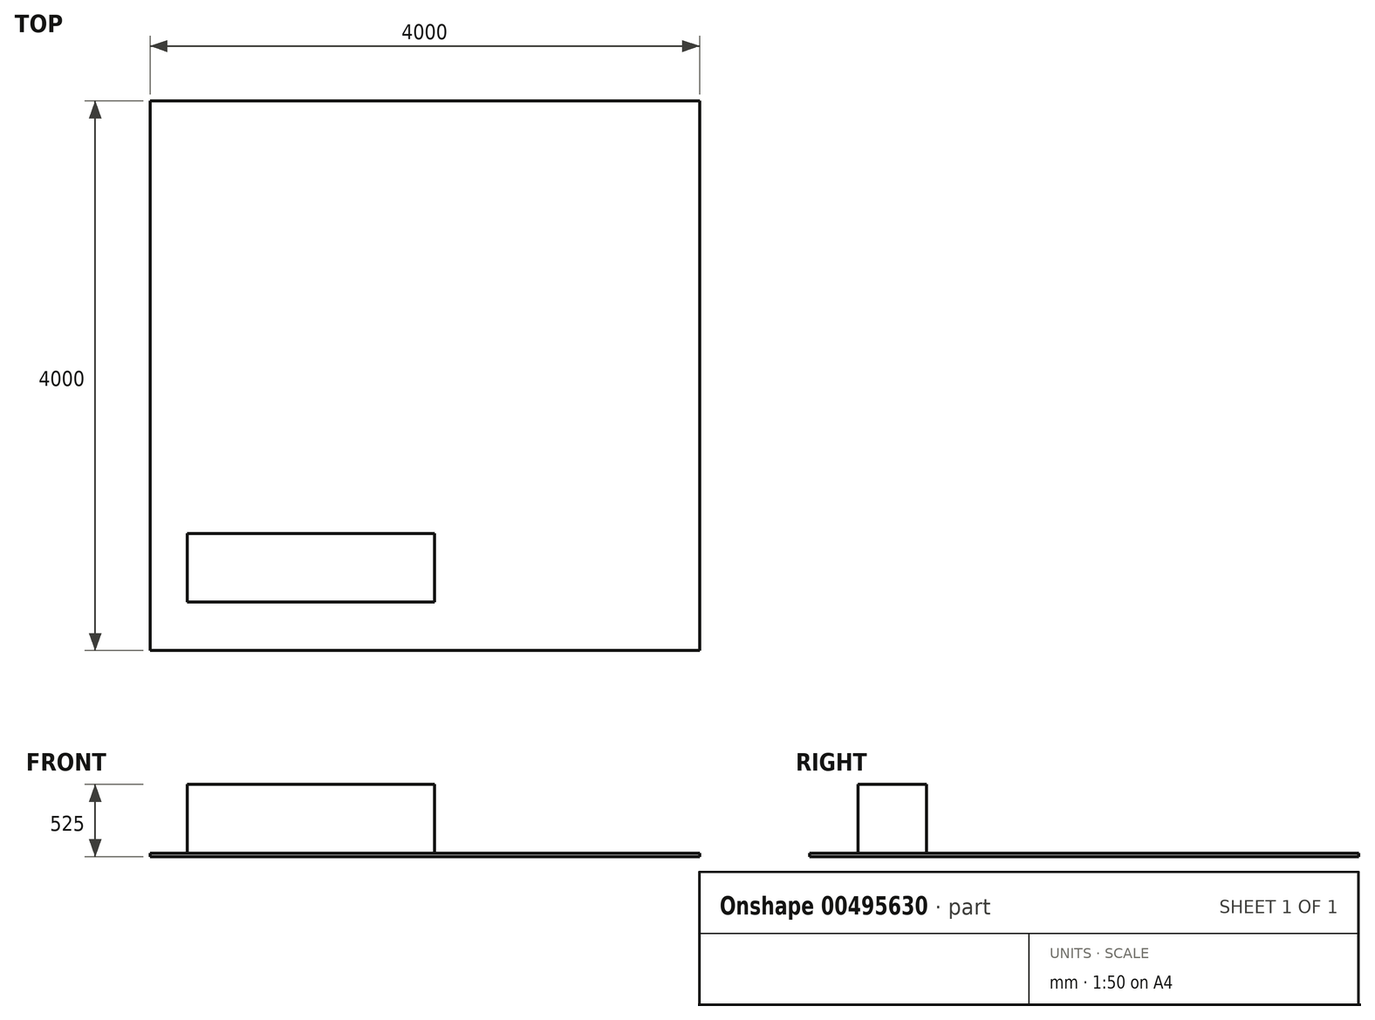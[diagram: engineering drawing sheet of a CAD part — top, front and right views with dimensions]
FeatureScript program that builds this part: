
annotation { "Feature Type Name" : "Feature", "Feature Type Description" : "" }
export const myFeature = defineFeature(function(context is Context, id is Id, definition is map)
    precondition{}
    {
        {
            var Q0;
            Q0=qCreatedBy(makeId("Top.planeOp"),FACE);
            var sketch = newSketch(context, id + "F0", { "sketchPlane" : qUnion([Q0])});
            skLineSegment(sketch, "E0.bottom", {"start": v(2000, 2000) * mm, "end": v(-2000, 2000) * mm});
            skLineSegment(sketch, "E0.top", {"start": v(2000, -2000) * mm, "end": v(-2000, -2000) * mm});
            skLineSegment(sketch, "E0.left", {"start": v(2000, 2000) * mm, "end": v(2000, -2000) * mm});
            skLineSegment(sketch, "E0.right", {"start": v(-2000, 2000) * mm, "end": v(-2000, -2000) * mm});
            skPoint(sketch, "E0.middle", {"position": v(0, 0) * mm});
            skSolve(sketch);
        }
        {
            var Q0;
            Q0 = qSketchRegion(id + "F0", true);
            extrude(context, id + "F1", {"entities" : qUnion([Q0]), "depth" : 25 * mm});
        }
        {
            var Q0;
            Q0=makeQuery(id+"F1.opExtrude","CAP_FACE",FACE,{"disambiguationData":[OSD([sQuery(id+"F0.wireOp",EDGE,"E0.bottom"),sQuery(id+"F0.wireOp",EDGE,"E0.top"),sQuery(id+"F0.wireOp",EDGE,"E0.left"),sQuery(id+"F0.wireOp",EDGE,"E0.right")])],"isStart":false});
            var sketch = newSketch(context, id + "F2", { "sketchPlane" : qUnion([Q0])});
            skLineSegment(sketch, "E1.bottom", {"start": v(70.68, -1147.85) * mm, "end": v(-1729.32, -1147.85) * mm});
            skLineSegment(sketch, "E1.top", {"start": v(70.68, -1647.85) * mm, "end": v(-1729.32, -1647.85) * mm});
            skLineSegment(sketch, "E1.left", {"start": v(70.68, -1147.85) * mm, "end": v(70.68, -1647.85) * mm});
            skLineSegment(sketch, "E1.right", {"start": v(-1729.32, -1147.85) * mm, "end": v(-1729.32, -1647.85) * mm});
            skPoint(sketch, "E1.middle", {"position": v(-829.32, -1397.85) * mm});
            skSolve(sketch);
        }
        {
            var Q0;
            Q0 = qSketchRegion(id + "F2", true);
            extrude(context, id + "F3", {"entities" : qUnion([Q0]), "depth" : 500 * mm});
        }
    });
